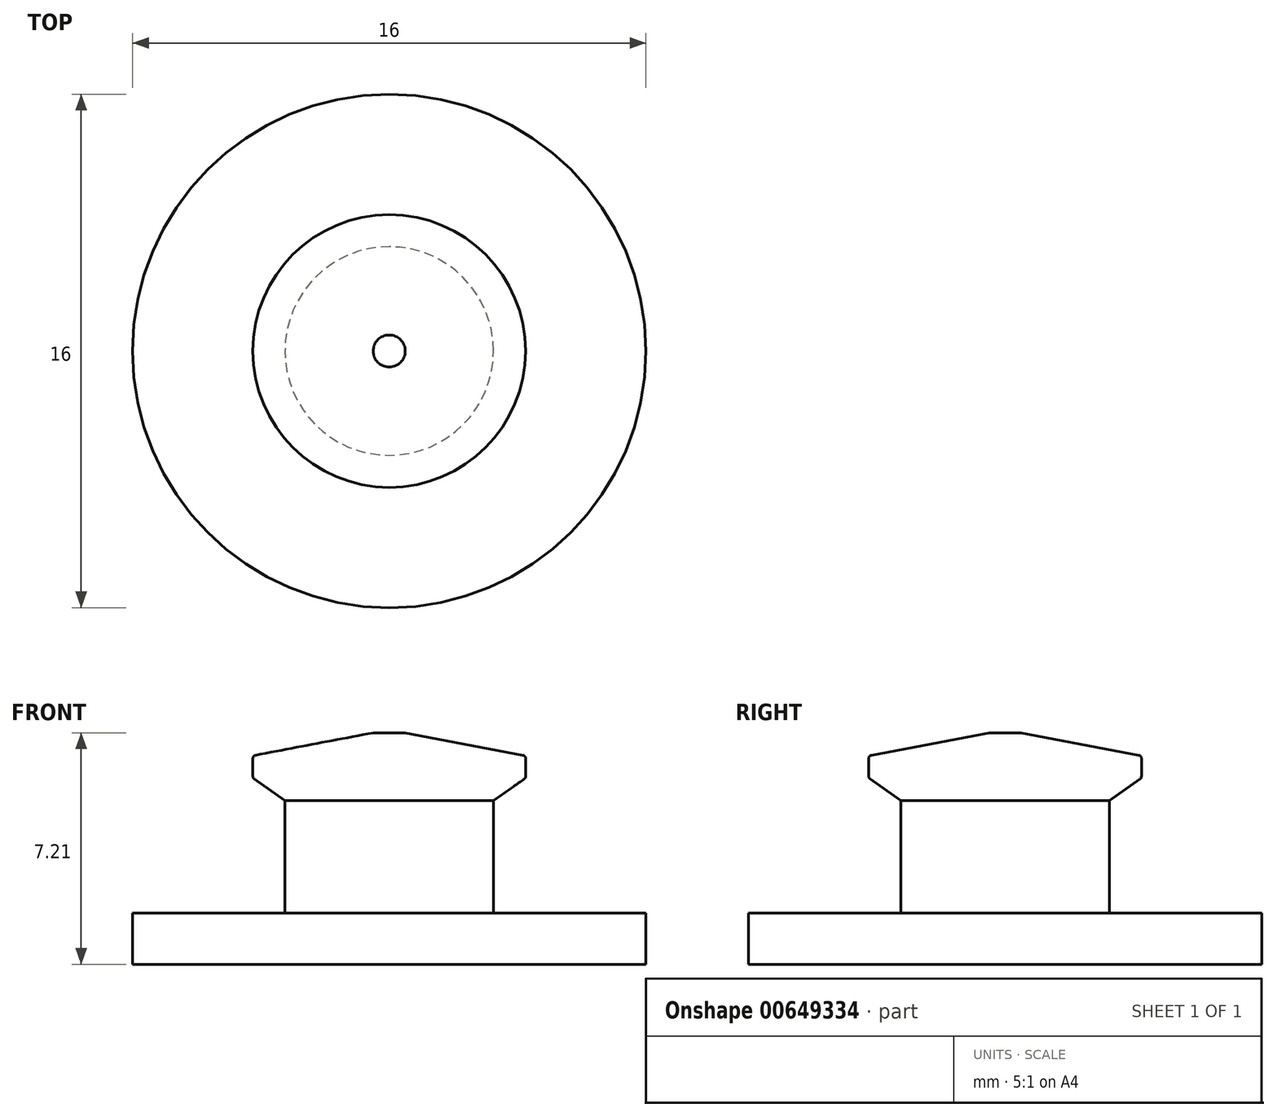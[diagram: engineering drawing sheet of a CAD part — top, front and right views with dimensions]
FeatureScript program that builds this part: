
annotation { "Feature Type Name" : "Feature", "Feature Type Description" : "" }
export const myFeature = defineFeature(function(context is Context, id is Id, definition is map)
    precondition{}
    {
        {
            var Q0;
            Q0=qCreatedBy(makeId("Right.planeOp"),FACE);
            var sketch = newSketch(context, id + "F0", { "sketchPlane" : qUnion([Q0])});
            skLineSegment(sketch, "E0", {"start": v(0, 0) * mm, "end": v(8, 0) * mm});
            skLineSegment(sketch, "E1", {"start": v(8, 0) * mm, "end": v(8, 1.6) * mm});
            skLineSegment(sketch, "E2", {"start": v(8, 1.6) * mm, "end": v(0, 1.6) * mm});
            skLineSegment(sketch, "E3", {"start": v(3.25, 1.6) * mm, "end": v(3.25, 5.1) * mm});
            skLineSegment(sketch, "E4", {"start": v(0, 7.21) * mm, "end": v(0.5, 7.21) * mm});
            skLineSegment(sketch, "E5", {"start": v(0.5, 7.21) * mm, "end": v(4.25, 6.5) * mm});
            skLineSegment(sketch, "E6", {"start": v(0, 7.21) * mm, "end": v(0, 0) * mm});
            skLineSegment(sketch, "E7", {"start": v(3.25, 5.1) * mm, "end": v(4.25, 5.8) * mm});
            skLineSegment(sketch, "E8", {"start": v(4.25, 5.8) * mm, "end": v(4.25, 6.5) * mm});
            skSolve(sketch);
        }
        {
            var Q0;
            {var subQ0=sQuery(id+"F0.wireOp",EDGE,"E3");Q0=makeQuery(id+"F0.imprint","IMPRINT",FACE,{"disambiguationData":[TD([[makeQuery(id+"F0.imprint","IMPRINT",EDGE,{"derivedFrom":subQ0}),1.0]])]});}
            var Q1;
            {var subQ5=sQuery(id+"F0.wireOp",EDGE,"E0");Q1=makeQuery(id+"F0.imprint","IMPRINT",FACE,{"disambiguationData":[TD([[makeQuery(id+"F0.imprint","IMPRINT",EDGE,{"derivedFrom":subQ5}),1.0]])]});}
            var Q2;
            Q2=sQuery(id+"F0.wireOp",EDGE,"E6");
            revolve(context, id + "F1", {"entities" : qUnion([Q0, Q1]), "axis" : qUnion([Q2]), "revolveType" : RevolveType.FULL});
        }
        {
            var Q0;
            Q0=makeQuery(id+"F1.opRevolve","SWEPT_EDGE",EDGE,{"disambiguationData":[OSD([sQuery(id+"F0.wireOp",EDGE,"E5"),sQuery(id+"F0.wireOp",EDGE,"E8")])]});
            var Q1;
            Q1=makeQuery(id+"F1.opRevolve","SWEPT_EDGE",EDGE,{"disambiguationData":[OSD([sQuery(id+"F0.wireOp",EDGE,"E7"),sQuery(id+"F0.wireOp",EDGE,"E8")])]});
            fillet(context, id + "F2", {"entities" : qUnion([Q0, Q1]), "radius" : 0.1 * mm, "tangentPropagation" : true, "allowEdgeOverflow" : false});
        }
    });
